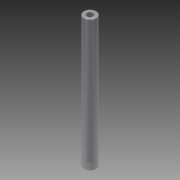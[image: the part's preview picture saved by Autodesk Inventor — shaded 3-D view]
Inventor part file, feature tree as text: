
AUTODESK INVENTOR PART (.ipt)
format: ipt  version: 2013 (Build 170138000, 138)  size: 81,408 bytes
history: native  units: mm
features: extrude x1, sketch x1
ambient origin geometry x8: Origin, YZ Plane, XZ Plane, XY Plane, X Axis, Y Axis, Z Axis, Center Point
bodies: Solid1 (feature_tree)
feature tree (2):
  extrude  "Extrusion1"  Depth=4.0mm
  sketch  "Sketch1"  dims[d0=2.0mm d2=4.0mm d3=42.0mm d4=0.0mm]
